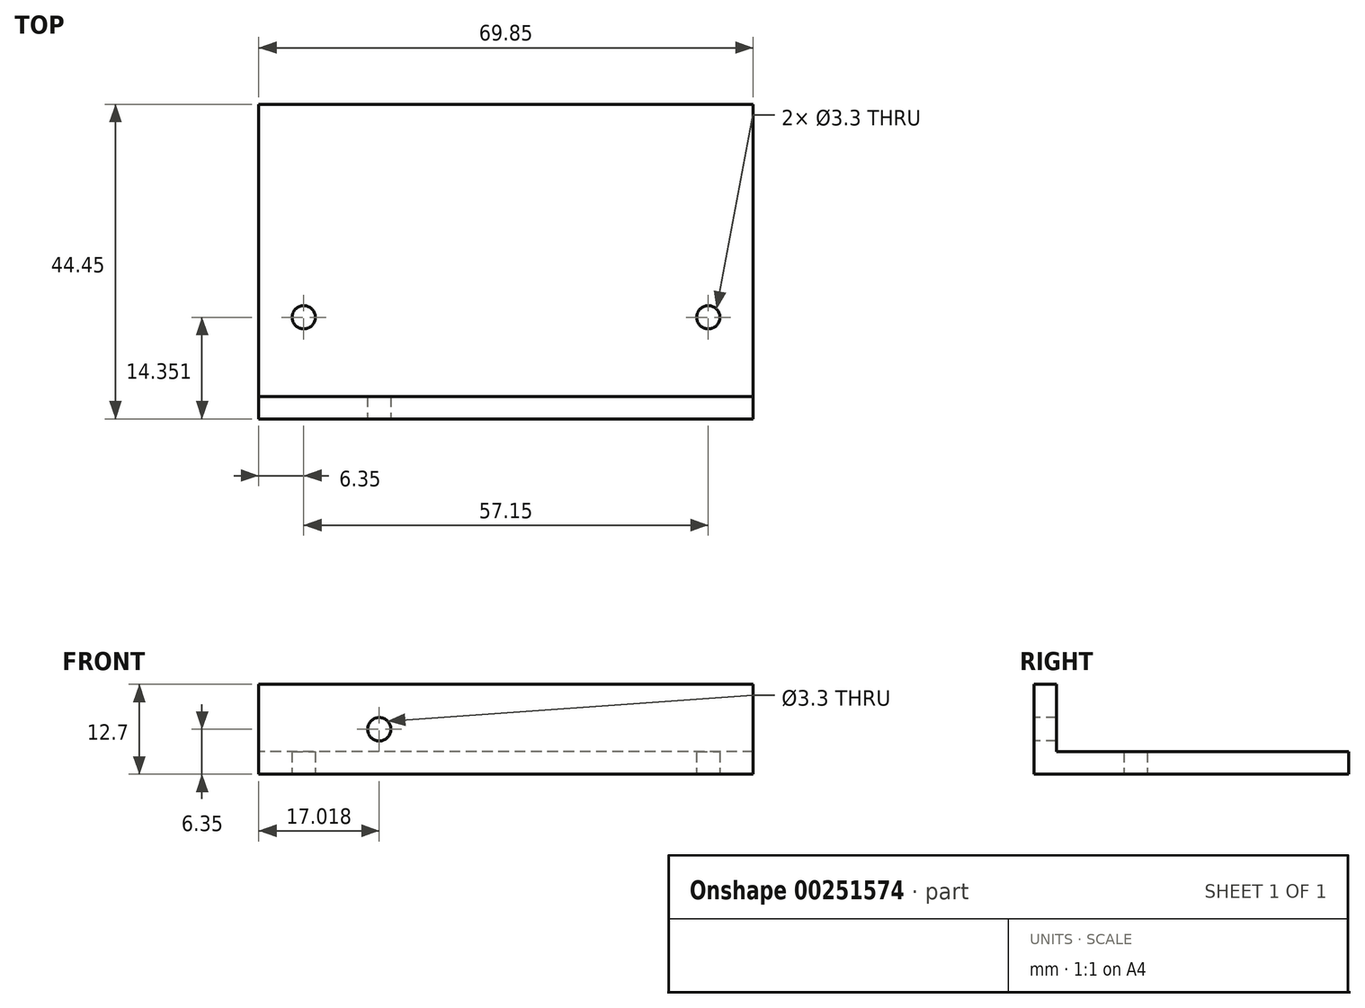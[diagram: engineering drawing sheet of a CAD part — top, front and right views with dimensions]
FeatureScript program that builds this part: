
annotation { "Feature Type Name" : "Feature", "Feature Type Description" : "" }
export const myFeature = defineFeature(function(context is Context, id is Id, definition is map)
    precondition{}
    {
        {
            var Q0;
            Q0=qCreatedBy(makeId("Right.planeOp"),FACE);
            var sketch = newSketch(context, id + "F0", { "sketchPlane" : qUnion([Q0])});
            skLineSegment(sketch, "E0", {"start": v(0, 0) * mm, "end": v(44.45, 0) * mm});
            skLineSegment(sketch, "E1", {"start": v(44.45, 0) * mm, "end": v(44.45, 3.18) * mm});
            skLineSegment(sketch, "E2", {"start": v(44.45, 3.18) * mm, "end": v(3.17, 3.18) * mm});
            skLineSegment(sketch, "E3", {"start": v(3.17, 3.18) * mm, "end": v(3.17, 12.7) * mm});
            skLineSegment(sketch, "E4", {"start": v(3.17, 12.7) * mm, "end": v(0, 12.7) * mm});
            skLineSegment(sketch, "E5", {"start": v(0, 12.7) * mm, "end": v(0, 0) * mm});
            skSolve(sketch);
        }
        {
            var Q0;
            Q0 = qSketchRegion(id + "F0", true);
            extrude(context, id + "F1", {"entities" : qUnion([Q0]), "depth" : 69.85 * mm});
        }
        {
            var Q0;
            Q0=makeQuery(id+"F1.opExtrude","SWEPT_FACE",FACE,{"disambiguationData":[OSD([sQuery(id+"F0.wireOp",EDGE,"E0")])]});
            var sketch = newSketch(context, id + "F2", { "sketchPlane" : qUnion([Q0])});
            skPoint(sketch, "E6", {"position": v(6.35, -14.35) * mm});
            skPoint(sketch, "E7", {"position": v(63.5, -14.35) * mm});
            skSolve(sketch);
        }
        {
            var Q0;
            Q0=sQuery(id+"F2.wireOp",VERTEX,"E6");
            var Q1;
            Q1=sQuery(id+"F2.wireOp",VERTEX,"E7");
            var Q2;
            Q2=makeQuery(id+"F1.opExtrude","SWEPT_BODY",BODY,{"disambiguationData":[OSD([sQuery(id+"F0.wireOp",EDGE,"E0"),sQuery(id+"F0.wireOp",EDGE,"E1"),sQuery(id+"F0.wireOp",EDGE,"E2"),sQuery(id+"F0.wireOp",EDGE,"E3"),sQuery(id+"F0.wireOp",EDGE,"E4"),sQuery(id+"F0.wireOp",EDGE,"E5")])]});
            hole(context, id + "F3", {"style" : HoleStyle.SIMPLE, "endStyle" : HoleEndStyle.THROUGH, "holeDiameter" : 3.3 * mm, "tappedDepth" : 12.7 * mm, "tapClearance" : 3, "startFromSketch" : true, "locations" : qUnion([Q0, Q1]), "scope" : qUnion([Q2])});
        }
        {
            var Q0;
            Q0=makeQuery(id+"F1.opExtrude","SWEPT_FACE",FACE,{"disambiguationData":[OSD([sQuery(id+"F0.wireOp",EDGE,"E5")])]});
            var sketch = newSketch(context, id + "F4", { "sketchPlane" : qUnion([Q0])});
            skPoint(sketch, "E8", {"position": v(17.02, 6.35) * mm});
            skSolve(sketch);
        }
        {
            var Q0;
            Q0=sQuery(id+"F4.wireOp",VERTEX,"E8");
            var Q1;
            Q1=makeQuery(id+"F1.opExtrude","SWEPT_BODY",BODY,{"disambiguationData":[OSD([sQuery(id+"F0.wireOp",EDGE,"E0"),sQuery(id+"F0.wireOp",EDGE,"E1"),sQuery(id+"F0.wireOp",EDGE,"E2"),sQuery(id+"F0.wireOp",EDGE,"E3"),sQuery(id+"F0.wireOp",EDGE,"E4"),sQuery(id+"F0.wireOp",EDGE,"E5")])]});
            hole(context, id + "F5", {"style" : HoleStyle.SIMPLE, "endStyle" : HoleEndStyle.THROUGH, "holeDiameter" : 3.3 * mm, "tappedDepth" : 12.7 * mm, "tapClearance" : 3, "startFromSketch" : true, "locations" : qUnion([Q0]), "scope" : qUnion([Q1])});
        }
    });
